# Revit family: 55005_HOST_FACE
name_source: partatom
category: Lighting Fixtures
units: mm (PartAtom-declared; Revit-internal decimal feet)

## family parameters
Cut with Voids When Loaded = Yes
Host = Face
Light Source = Yes
Part Type = Normal
Room Calculation Point = Yes
Round Connector Dimension = Use Diameter
Shared = No

## types (2) — shared parameters
AC/DC = AC/DC
Ambient_temperature = 25 °C
Apparent Load = 0 VA
BEGA_dummy = No
BEGA_internal = Yes
BEGA_internal_off = Yes
BEGA_internal_on = Yes
BEGA_internal_structure = Yes
CE_conformity = yes
Color Filter = 16777215
Colour_rendering_index = CRI > 80
Colour_temperature = 3000 K
Connecting_cable = 5.0 m H05RN-F 3 G 1²
Custom_made_product = No
Description = Garden luminaire
Description_custom_made_product = Here you can specify modifications of your custom-made product
Dimming Lamp Color Temperature Shift = <None>
ENEC = yes
Energy_efficiency_class = LED A++ - A
Frequency = 0/50-60 Hz
LED_module_designation = LED-0684/830
Lamp = LED 3.2 W
Lamp_luminous_flux = 295 lm
Load_Classification = Lighting
Logo = BEGA_Logo.png
Luminaire_luminous_flux = 186 lm
M_G = Yes
Manufacturer = BEGA
Material_11 = BEGA_glass_opal
Model = 55005
Order_number = 55005K3
Product_data_sheet = http://www.bega.de
Protection_class = IP 65
Safety_class = I
Service_life_criteria = L70B50 @ 25 °C = 400000 h
Tilt Angle = 0,00°
Type Image = 55005.png
URL = http://www.bega.de
Update = 2019-07-08T04:00:16
Voltage = 240 V
Weight = 1.05 kg
zero-valued in all types: Default Elevation

## per-type parameters (varying)
| type | Photometric Web File |
| BEGA_55005_graphite_K3 | 55005.ies |
| Garden Luminaire | 55005K3.ies |

## geometry (parser evidence)
native form markers: Sweep x2
no freeform markers — native parametric forms only
